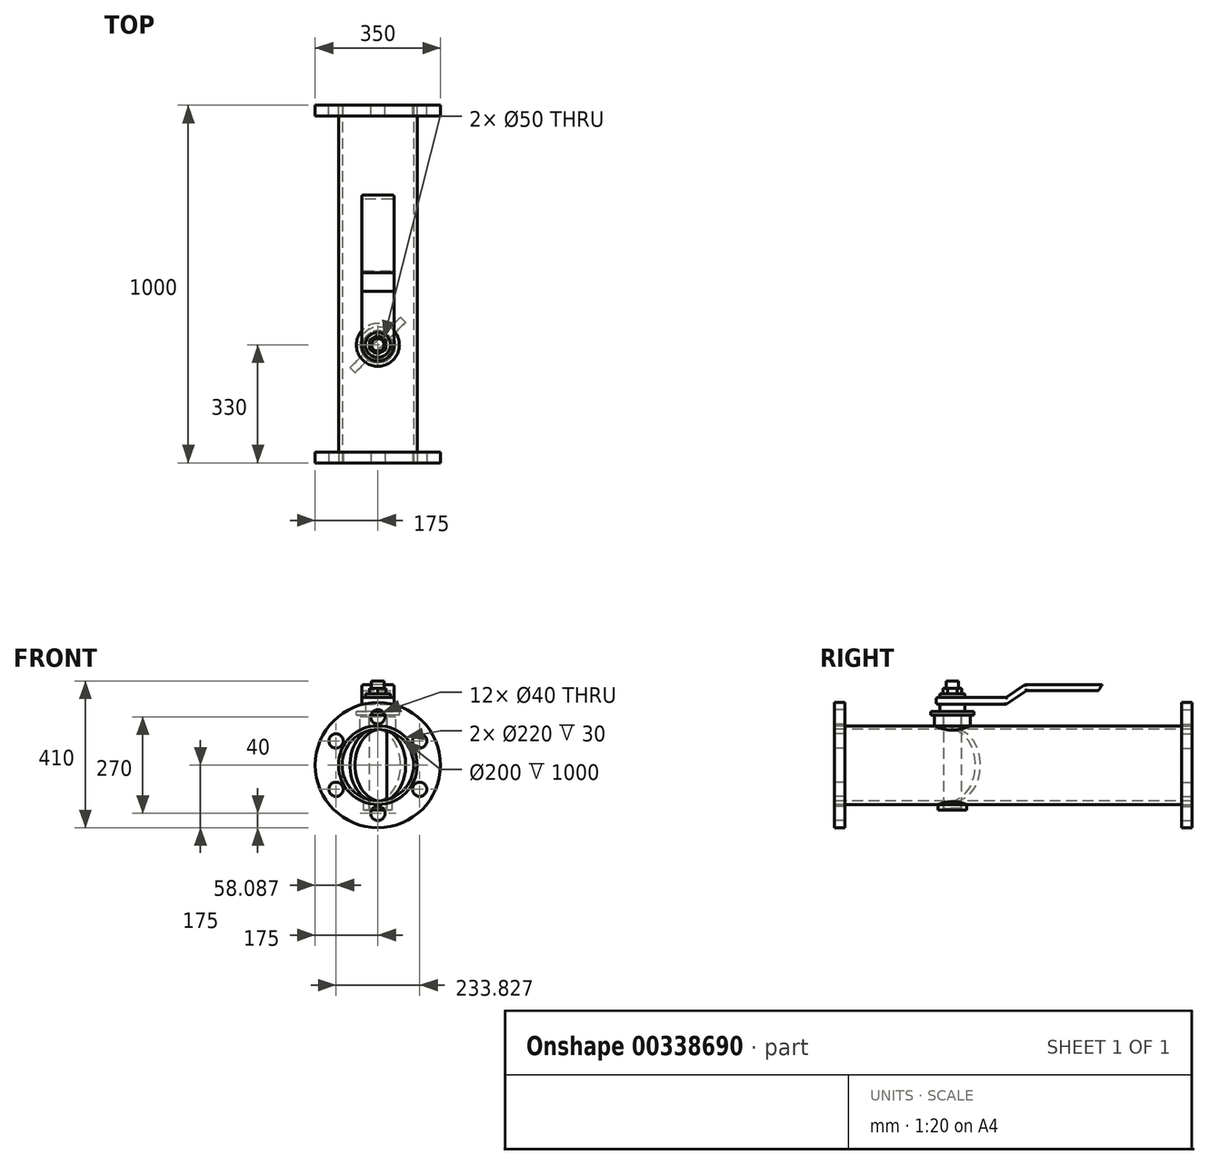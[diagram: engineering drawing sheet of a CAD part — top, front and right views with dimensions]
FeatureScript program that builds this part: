
annotation { "Feature Type Name" : "Feature", "Feature Type Description" : "" }
export const myFeature = defineFeature(function(context is Context, id is Id, definition is map)
    precondition{}
    {
        {
            var Q0;
            Q0=qCreatedBy(makeId("Front.planeOp"),FACE);
            var sketch = newSketch(context, id + "F0", { "sketchPlane" : qUnion([Q0])});
            skCircle(sketch, "E0", {"center": v(0, 0) * mm, "radius": 110 * mm});
            skSolve(sketch);
        }
        {
            var Q0;
            Q0=makeQuery(id+"F0.imprint","IMPRINT",FACE,{"disambiguationData":[TD([[makeQuery(id+"F0.imprint","IMPRINT",EDGE,{"derivedFrom":sQuery(id+"F0.wireOp",EDGE,"E0")}),1.0]])]});
            extrude(context, id + "F1", {"entities" : qUnion([Q0]), "oppositeDirection" : true, "depth" : 1000 * mm});
        }
        {
            var Q0;
            Q0=makeQuery(id+"F1.opExtrude","CAP_FACE",FACE,{"disambiguationData":[OSD([sQuery(id+"F0.wireOp",EDGE,"E0")])],"isStart":true});
            var sketch = newSketch(context, id + "F2", { "sketchPlane" : qUnion([Q0])});
            skCircle(sketch, "E1", {"center": v(0, 0) * mm, "radius": 175 * mm});
            skSolve(sketch);
        }
        {
            var Q0;
            Q0=makeQuery(id+"F2.imprint","IMPRINT",FACE,{"disambiguationData":[TD([[makeQuery(id+"F2.imprint","IMPRINT",EDGE,{"derivedFrom":sQuery(id+"F2.wireOp",EDGE,"E1")}),1.0]])]});
            extrude(context, id + "F3", {"entities" : qUnion([Q0]), "oppositeDirection" : true, "depth" : 30 * mm});
        }
        {
            var Q0;
            Q0=makeQuery(id+"F1.opExtrude","CAP_FACE",FACE,{"disambiguationData":[OSD([sQuery(id+"F0.wireOp",EDGE,"E0")])],"isStart":false});
            var sketch = newSketch(context, id + "F4", { "sketchPlane" : qUnion([Q0])});
            skCircle(sketch, "E2", {"center": v(0, 0) * mm, "radius": 175 * mm});
            skSolve(sketch);
        }
        {
            var Q0;
            Q0=makeQuery(id+"F4.imprint","IMPRINT",FACE,{"disambiguationData":[TD([[makeQuery(id+"F4.imprint","IMPRINT",EDGE,{"derivedFrom":sQuery(id+"F4.wireOp",EDGE,"E2")}),1.0]])]});
            extrude(context, id + "F5", {"entities" : qUnion([Q0]), "oppositeDirection" : true, "depth" : 30 * mm});
        }
        {
            var Q0;
            Q0=makeQuery(id+"F3.opExtrude","CAP_FACE",FACE,{"disambiguationData":[OSD([sQuery(id+"F0.wireOp",EDGE,"E0"),sQuery(id+"F2.wireOp",EDGE,"E1")])],"isStart":true});
            var sketch = newSketch(context, id + "F6", { "sketchPlane" : qUnion([Q0])});
            skCircle(sketch, "E3", {"center": v(0, 0) * mm, "radius": 100 * mm});
            skSolve(sketch);
        }
        {
            var Q0;
            Q0=makeQuery(id+"F6.imprint","IMPRINT",FACE,{"disambiguationData":[TD([[makeQuery(id+"F6.imprint","IMPRINT",EDGE,{"derivedFrom":sQuery(id+"F6.wireOp",EDGE,"E3")}),1.0]])]});
            extrude(context, id + "F7", {"entities" : qUnion([Q0]), "operationType" : NewBodyOperationType.REMOVE, "endBound" : BoundingType.THROUGH_ALL, "oppositeDirection" : true, "depth" : 25 * mm});
        }
        {
            var Q0;
            Q0=makeQuery(id+"F2.imprint","IMPRINT",FACE,{"disambiguationData":[TD([[makeQuery(id+"F2.imprint","IMPRINT",EDGE,{"derivedFrom":sQuery(id+"F2.wireOp",EDGE,"E1")}),1.0]])]});
            var sketch = newSketch(context, id + "F8", { "sketchPlane" : qUnion([Q0])});
            skCircle(sketch, "E4", {"center": v(0, 135) * mm, "radius": 20 * mm});
            skCircle(sketch, "E5.1.0", {"center": v(-116.91, 67.5) * mm, "radius": 20 * mm});
            skCircle(sketch, "E5.2.0", {"center": v(-116.91, -67.5) * mm, "radius": 20 * mm});
            skCircle(sketch, "E5.3.0", {"center": v(0, -135) * mm, "radius": 20 * mm});
            skCircle(sketch, "E5.4.0", {"center": v(116.91, -67.5) * mm, "radius": 20 * mm});
            skCircle(sketch, "E5.5.0", {"center": v(116.91, 67.5) * mm, "radius": 20 * mm});
            skPoint(sketch, "E5.center", {"position": v(0, 0) * mm});
            skSolve(sketch);
        }
        {
            var Q0;
            Q0 = qSketchRegion(id + "F8", true);
            var Q1;
            Q1=makeQuery(id+"F3.opExtrude","CAP_FACE",FACE,{"disambiguationData":[OSD([sQuery(id+"F0.wireOp",EDGE,"E0"),sQuery(id+"F2.wireOp",EDGE,"E1")])],"isStart":false});
            extrude(context, id + "F9", {"entities" : qUnion([Q0]), "operationType" : NewBodyOperationType.REMOVE, "endBound" : BoundingType.UP_TO_SURFACE, "oppositeDirection" : true, "endBoundEntityFace" : qUnion([Q1]), "depth" : 25 * mm});
        }
        {
            var Q0;
            Q0=makeQuery(id+"F4.imprint","IMPRINT",FACE,{"disambiguationData":[TD([[makeQuery(id+"F4.imprint","IMPRINT",EDGE,{"derivedFrom":sQuery(id+"F4.wireOp",EDGE,"E2")}),1.0]])]});
            var sketch = newSketch(context, id + "F10", { "sketchPlane" : qUnion([Q0])});
            skCircle(sketch, "E6", {"center": v(0, 135) * mm, "radius": 20 * mm});
            skCircle(sketch, "E7.1.0", {"center": v(-116.91, 67.5) * mm, "radius": 20 * mm});
            skCircle(sketch, "E7.2.0", {"center": v(-116.91, -67.5) * mm, "radius": 20 * mm});
            skCircle(sketch, "E7.3.0", {"center": v(0, -135) * mm, "radius": 20 * mm});
            skCircle(sketch, "E7.4.0", {"center": v(116.91, -67.5) * mm, "radius": 20 * mm});
            skCircle(sketch, "E7.5.0", {"center": v(116.91, 67.5) * mm, "radius": 20 * mm});
            skPoint(sketch, "E7.center", {"position": v(0, 0) * mm});
            skSolve(sketch);
        }
        {
            var Q0;
            Q0 = qSketchRegion(id + "F10", true);
            var Q1;
            Q1=makeQuery(id+"F5.opExtrude","CAP_FACE",FACE,{"disambiguationData":[OSD([sQuery(id+"F0.wireOp",EDGE,"E0"),sQuery(id+"F4.wireOp",EDGE,"E2")])],"isStart":false});
            extrude(context, id + "F11", {"entities" : qUnion([Q0]), "operationType" : NewBodyOperationType.REMOVE, "endBound" : BoundingType.UP_TO_SURFACE, "oppositeDirection" : true, "endBoundEntityFace" : qUnion([Q1]), "depth" : 25 * mm});
        }
        {
            var Q0;
            Q0=qCreatedBy(makeId("Front.planeOp"),FACE);
            cPlane(context, id + "F12", {"entities" : qUnion([Q0]), "cplaneType" : CPlaneType.OFFSET, "offset" : 330 * mm, "oppositeDirection" : true, "width" : 150 * mm, "height" : 150 * mm});
        }
        {
            var Q0;
            Q0=qCreatedBy(id+"F12.planeOp",FACE);
            var sketch = newSketch(context, id + "F13", { "sketchPlane" : qUnion([Q0])});
            skCircle(sketch, "E8", {"center": v(0, 0) * mm, "radius": 100 * mm});
            skSolve(sketch);
        }
        {
            var Q0;
            Q0 = qSketchRegion(id + "F13", true);
            extrude(context, id + "F14", {"entities" : qUnion([Q0]), "depth" : 10 * mm, "hasSecondDirection" : true, "secondDirectionOppositeDirection" : true, "secondDirectionDepth" : 10 * mm});
        }
        {
            var Q0;
            Q0=qCreatedBy(makeId("Top.planeOp"),FACE);
            var sketch = newSketch(context, id + "F15", { "sketchPlane" : qUnion([Q0])});
            skCircle(sketch, "E9", {"center": v(0, 330) * mm, "radius": 25 * mm});
            skSolve(sketch);
        }
        {
            var Q0;
            Q0 = qSketchRegion(id + "F15", true);
            extrude(context, id + "F16", {"entities" : qUnion([Q0]), "depth" : 150 * mm, "hasSecondDirection" : true, "secondDirectionOppositeDirection" : true, "secondDirectionDepth" : 120 * mm});
        }
        {
            var Q0;
            Q0=makeQuery(id+"F16.opExtrude","CAP_FACE",FACE,{"disambiguationData":[OSD([sQuery(id+"F15.wireOp",EDGE,"E9")])],"isStart":true});
            var sketch = newSketch(context, id + "F17", { "sketchPlane" : qUnion([Q0])});
            skCircle(sketch, "E10", {"center": v(0, -330) * mm, "radius": 40 * mm});
            skSolve(sketch);
        }
        {
            var Q0;
            Q0=makeQuery(id+"F17.imprint","IMPRINT",FACE,{"disambiguationData":[TD([[makeQuery(id+"F17.imprint","IMPRINT",EDGE,{"derivedFrom":sQuery(id+"F17.wireOp",EDGE,"E10")}),1.0]])]});
            var Q1;
            Q1=makeQuery(id+"F1.opExtrude","SWEPT_FACE",FACE,{"disambiguationData":[OSD([sQuery(id+"F0.wireOp",EDGE,"E0")])]});
            extrude(context, id + "F18", {"entities" : qUnion([Q0]), "depth" : 5 * mm, "hasSecondDirection" : true, "secondDirectionBound" : SecondDirectionBoundingType.UP_TO_SURFACE, "secondDirectionOppositeDirection" : true, "secondDirectionBoundEntityFace" : qUnion([Q1]), "secondDirectionDepth" : 25 * mm});
        }
        {
            var Q0;
            Q0=makeQuery(id+"F16.opExtrude","CAP_FACE",FACE,{"disambiguationData":[OSD([sQuery(id+"F15.wireOp",EDGE,"E9")])],"isStart":false});
            var sketch = newSketch(context, id + "F19", { "sketchPlane" : qUnion([Q0])});
            skCircle(sketch, "E11", {"center": v(0, 330) * mm, "radius": 60 * mm});
            skSolve(sketch);
        }
        {
            var Q0;
            Q0=makeQuery(id+"F19.imprint","IMPRINT",FACE,{"disambiguationData":[TD([[makeQuery(id+"F19.imprint","IMPRINT",EDGE,{"derivedFrom":sQuery(id+"F19.wireOp",EDGE,"E11")}),1.0]])]});
            extrude(context, id + "F20", {"entities" : qUnion([Q0]), "operationType" : NewBodyOperationType.ADD, "oppositeDirection" : true, "depth" : 10 * mm});
        }
        {
            var Q0;
            Q0=makeQuery(id+"F20.opExtrude","CAP_FACE",FACE,{"disambiguationData":[OSD([sQuery(id+"F15.wireOp",EDGE,"E9"),sQuery(id+"F19.wireOp",EDGE,"E11")])],"isStart":false});
            var sketch = newSketch(context, id + "F21", { "sketchPlane" : qUnion([Q0])});
            skCircle(sketch, "E12", {"center": v(0, -330) * mm, "radius": 50 * mm});
            skSolve(sketch);
        }
        {
            var Q0;
            Q0=makeQuery(id+"F21.imprint","IMPRINT",FACE,{"disambiguationData":[TD([[makeQuery(id+"F21.imprint","IMPRINT",EDGE,{"derivedFrom":sQuery(id+"F21.wireOp",EDGE,"E12")}),1.0]])]});
            var Q1;
            Q1=makeQuery(id+"F1.opExtrude","SWEPT_FACE",FACE,{"disambiguationData":[OSD([sQuery(id+"F0.wireOp",EDGE,"E0")])]});
            extrude(context, id + "F22", {"entities" : qUnion([Q0]), "endBound" : BoundingType.UP_TO_SURFACE, "endBoundEntityFace" : qUnion([Q1]), "depth" : 25 * mm});
        }
        {
            var Q0;
            {var subQ0=sQuery(id+"F15.wireOp",EDGE,"E9");Q0=makeQuery(id+"F20.boolean.opBoolean","MERGE",FACE,{"derivedFrom":[makeQuery(id+"F16.opExtrude","CAP_FACE",FACE,{"disambiguationData":[OSD([subQ0])],"isStart":false}),makeQuery(id+"F20.opExtrude","CAP_FACE",FACE,{"disambiguationData":[OSD([subQ0,sQuery(id+"F19.wireOp",EDGE,"E11")])],"isStart":true})]});}
            var sketch = newSketch(context, id + "F23", { "sketchPlane" : qUnion([Q0])});
            skCircle(sketch, "E13", {"center": v(0, 330) * mm, "radius": 35 * mm});
            skSolve(sketch);
        }
        {
            var Q0;
            Q0=makeQuery(id+"F23.imprint","IMPRINT",FACE,{"disambiguationData":[TD([[makeQuery(id+"F23.imprint","IMPRINT",EDGE,{"derivedFrom":sQuery(id+"F23.wireOp",EDGE,"E13")}),1.0]])]});
            extrude(context, id + "F24", {"entities" : qUnion([Q0]), "operationType" : NewBodyOperationType.ADD, "depth" : 50 * mm});
        }
        {
            var Q0;
            Q0=makeQuery(id+"F24.opExtrude","CAP_FACE",FACE,{"disambiguationData":[OSD([sQuery(id+"F23.wireOp",EDGE,"E13")])],"isStart":false});
            var sketch = newSketch(context, id + "F25", { "sketchPlane" : qUnion([Q0])});
            skCircle(sketch, "E14", {"center": v(0, 330) * mm, "radius": 17.5 * mm});
            skSolve(sketch);
        }
        {
            var Q0;
            Q0=makeQuery(id+"F25.imprint","IMPRINT",FACE,{"disambiguationData":[TD([[makeQuery(id+"F25.imprint","IMPRINT",EDGE,{"derivedFrom":sQuery(id+"F25.wireOp",EDGE,"E14")}),1.0]])]});
            extrude(context, id + "F26", {"entities" : qUnion([Q0]), "operationType" : NewBodyOperationType.ADD, "depth" : 35 * mm});
        }
        {
            var Q0;
            Q0=makeQuery(id+"F24.opExtrude","CAP_FACE",FACE,{"disambiguationData":[OSD([sQuery(id+"F23.wireOp",EDGE,"E13")])],"isStart":false});
            var sketch = newSketch(context, id + "F27", { "sketchPlane" : qUnion([Q0])});
            skCircle(sketch, "E15.cCircle", {"center": v(0, 330) * mm, "radius": 22.6 * mm, "construction": true});
            skLineSegment(sketch, "E15.0", {"start": v(-22.6, 316.96) * mm, "end": v(-22.6, 343.04) * mm});
            skLineSegment(sketch, "E15.1", {"start": v(-22.6, 343.04) * mm, "end": v(0, 356.09) * mm});
            skLineSegment(sketch, "E15.2", {"start": v(0, 356.09) * mm, "end": v(22.6, 343.04) * mm});
            skLineSegment(sketch, "E15.3", {"start": v(22.6, 343.04) * mm, "end": v(22.6, 316.96) * mm});
            skLineSegment(sketch, "E15.4", {"start": v(22.6, 316.96) * mm, "end": v(0, 303.91) * mm});
            skLineSegment(sketch, "E15.5", {"start": v(0, 303.91) * mm, "end": v(-22.6, 316.96) * mm});
            skPoint(sketch, "E15.0.midPoint", {"position": v(-22.6, 330) * mm});
            skSolve(sketch);
        }
        {
            var Q0;
            Q0=makeQuery(id+"F27.imprint","IMPRINT",FACE,{"disambiguationData":[TD([[makeQuery(id+"F27.imprint","IMPRINT",EDGE,{"derivedFrom":sQuery(id+"F27.wireOp",EDGE,"E15.0")}),-1.0]])]});
            extrude(context, id + "F28", {"entities" : qUnion([Q0]), "operationType" : NewBodyOperationType.ADD, "depth" : 15 * mm});
        }
        {
            var Q0;
            {var subQ0=sQuery(id+"F15.wireOp",EDGE,"E9");Q0=makeQuery(id+"F20.boolean.opBoolean","MERGE",FACE,{"derivedFrom":[makeQuery(id+"F16.opExtrude","CAP_FACE",FACE,{"disambiguationData":[OSD([subQ0])],"isStart":false}),makeQuery(id+"F20.opExtrude","CAP_FACE",FACE,{"disambiguationData":[OSD([subQ0,sQuery(id+"F19.wireOp",EDGE,"E11")])],"isStart":true})]});}
            cPlane(context, id + "F29", {"entities" : qUnion([Q0]), "cplaneType" : CPlaneType.OFFSET, "offset" : 20 * mm, "width" : 150 * mm, "height" : 150 * mm});
        }
        {
            var Q0;
            Q0=qCreatedBy(id+"F29.planeOp",FACE);
            var sketch = newSketch(context, id + "F30", { "sketchPlane" : qUnion([Q0])});
            skArc(sketch, "E16", {"start": v(-45, 330) * mm, "mid": v(0, 285) * mm, "end": v(45, 330) * mm});
            skLineSegment(sketch, "E17", {"start": v(45, 330) * mm, "end": v(45, 480) * mm});
            skLineSegment(sketch, "E18", {"start": v(45, 480) * mm, "end": v(-45, 480) * mm});
            skLineSegment(sketch, "E19", {"start": v(-45, 480) * mm, "end": v(-45, 330) * mm});
            skSolve(sketch);
        }
        {
            var Q0;
            Q0=makeQuery(id+"F30.imprint","IMPRINT",FACE,{"disambiguationData":[TD([[makeQuery(id+"F30.imprint","IMPRINT",EDGE,{"derivedFrom":sQuery(id+"F30.wireOp",EDGE,"E16")}),1.0]])]});
            extrude(context, id + "F31", {"entities" : qUnion([Q0]), "operationType" : NewBodyOperationType.ADD, "depth" : 20 * mm});
        }
        {
            var Q0;
            Q0=makeQuery(id+"F31.opExtrude","SWEPT_FACE",FACE,{"disambiguationData":[OSD([sQuery(id+"F30.wireOp",EDGE,"E17")])]});
            var sketch = newSketch(context, id + "F32", { "sketchPlane" : qUnion([Q0])});
            skLineSegment(sketch, "E20", {"start": v(480, 190) * mm, "end": v(532.26, 224.92) * mm});
            skLineSegment(sketch, "E21", {"start": v(532.26, 224.92) * mm, "end": v(748.87, 224.92) * mm});
            skSolve(sketch);
        }
        {
            var Q0;
            Q0=makeQuery(id+"F31.opExtrude","SWEPT_FACE",FACE,{"disambiguationData":[OSD([sQuery(id+"F30.wireOp",EDGE,"E18")])]});
            var Q1;
            Q1=sQuery(id+"F32.wireOp",EDGE,"E20");
            var Q2;
            Q2=sQuery(id+"F32.wireOp",EDGE,"E21");
            sweep(context, id + "F33", {"operationType" : NewBodyOperationType.ADD, "profiles" : qUnion([Q0]), "path" : qUnion([Q1, Q2])});
        }
        {
            var Q0;
            {var subQ0=sQuery(id+"F32.wireOp",EDGE,"E21");var subQ1=sQuery(id+"F30.wireOp",EDGE,"E18");var subQ2=sQuery(id+"F30.wireOp",EDGE,"E17");Q0=makeQuery(id+"F33.opSweep","SWEPT_EDGE",EDGE,{"disambiguationData":[OSD([subQ2,subQ1,subQ0]),TDD([makeQuery(id+"F31.opExtrude","CAP_VERTEX",VERTEX,{"disambiguationData":[OSD([subQ2,subQ1])],"isStart":false}),subQ0])]});}
            var Q1;
            {var subQ0=sQuery(id+"F32.wireOp",EDGE,"E20");var subQ1=sQuery(id+"F30.wireOp",EDGE,"E18");var subQ2=sQuery(id+"F30.wireOp",EDGE,"E17");Q1=makeQuery(id+"F33.opSweep","SWEPT_EDGE",EDGE,{"disambiguationData":[OSD([subQ2,subQ1,subQ0]),TDD([makeQuery(id+"F31.opExtrude","CAP_VERTEX",VERTEX,{"disambiguationData":[OSD([subQ2,subQ1])],"isStart":false}),subQ0])]});}
            var Q2;
            Q2=makeQuery(id+"F31.opExtrude","CAP_EDGE",EDGE,{"disambiguationData":[OSD([sQuery(id+"F30.wireOp",EDGE,"E17")])],"isStart":false});
            var Q3;
            Q3=makeQuery(id+"F31.opExtrude","CAP_EDGE",EDGE,{"disambiguationData":[OSD([sQuery(id+"F30.wireOp",EDGE,"E17")])],"isStart":true});
            var Q4;
            {var subQ0=sQuery(id+"F32.wireOp",EDGE,"E20");var subQ1=sQuery(id+"F30.wireOp",EDGE,"E18");var subQ2=sQuery(id+"F30.wireOp",EDGE,"E17");Q4=makeQuery(id+"F33.opSweep","SWEPT_EDGE",EDGE,{"disambiguationData":[OSD([subQ2,subQ1,subQ0]),TDD([makeQuery(id+"F31.opExtrude","CAP_VERTEX",VERTEX,{"disambiguationData":[OSD([subQ2,subQ1])],"isStart":true}),subQ0])]});}
            var Q5;
            {var subQ0=sQuery(id+"F32.wireOp",EDGE,"E21");var subQ1=sQuery(id+"F30.wireOp",EDGE,"E18");var subQ2=sQuery(id+"F30.wireOp",EDGE,"E17");Q5=makeQuery(id+"F33.opSweep","SWEPT_EDGE",EDGE,{"disambiguationData":[OSD([subQ2,subQ1,subQ0]),TDD([makeQuery(id+"F31.opExtrude","CAP_VERTEX",VERTEX,{"disambiguationData":[OSD([subQ2,subQ1])],"isStart":true}),subQ0])]});}
            var Q6;
            {var subQ0=sQuery(id+"F32.wireOp",EDGE,"E20");var subQ1=sQuery(id+"F30.wireOp",EDGE,"E19");var subQ2=sQuery(id+"F30.wireOp",EDGE,"E18");Q6=makeQuery(id+"F33.opSweep","SWEPT_EDGE",EDGE,{"disambiguationData":[OSD([subQ2,subQ1,subQ0]),TDD([makeQuery(id+"F31.opExtrude","CAP_VERTEX",VERTEX,{"disambiguationData":[OSD([subQ2,subQ1])],"isStart":false}),subQ0])]});}
            var Q7;
            {var subQ0=sQuery(id+"F32.wireOp",EDGE,"E21");var subQ1=sQuery(id+"F30.wireOp",EDGE,"E19");var subQ2=sQuery(id+"F30.wireOp",EDGE,"E18");Q7=makeQuery(id+"F33.opSweep","SWEPT_EDGE",EDGE,{"disambiguationData":[OSD([subQ2,subQ1,subQ0]),TDD([makeQuery(id+"F31.opExtrude","CAP_VERTEX",VERTEX,{"disambiguationData":[OSD([subQ2,subQ1])],"isStart":false}),subQ0])]});}
            var Q8;
            {var subQ0=sQuery(id+"F32.wireOp",EDGE,"E20");var subQ1=sQuery(id+"F30.wireOp",EDGE,"E19");var subQ2=sQuery(id+"F30.wireOp",EDGE,"E18");Q8=makeQuery(id+"F33.opSweep","SWEPT_EDGE",EDGE,{"disambiguationData":[OSD([subQ2,subQ1,subQ0]),TDD([makeQuery(id+"F31.opExtrude","CAP_VERTEX",VERTEX,{"disambiguationData":[OSD([subQ2,subQ1])],"isStart":true}),subQ0])]});}
            var Q9;
            {var subQ0=sQuery(id+"F32.wireOp",EDGE,"E21");var subQ1=sQuery(id+"F30.wireOp",EDGE,"E19");var subQ2=sQuery(id+"F30.wireOp",EDGE,"E18");Q9=makeQuery(id+"F33.opSweep","SWEPT_EDGE",EDGE,{"disambiguationData":[OSD([subQ2,subQ1,subQ0]),TDD([makeQuery(id+"F31.opExtrude","CAP_VERTEX",VERTEX,{"disambiguationData":[OSD([subQ2,subQ1])],"isStart":true}),subQ0])]});}
            fillet(context, id + "F34", {"entities" : qUnion([Q0, Q1, Q2, Q3, Q4, Q5, Q6, Q7, Q8, Q9]), "radius" : 5 * mm, "tangentPropagation" : true, "allowEdgeOverflow" : false});
        }
        {
            var Q0;
            Q0=qCreatedBy(makeId("Right.planeOp"),FACE);
            var sketch = newSketch(context, id + "F35", { "sketchPlane" : qUnion([Q0])});
            skLineSegment(sketch, "E22.0", {"start": v(312.5, 235) * mm, "end": v(347.5, 235) * mm, "construction": true});
            skPoint(sketch, "E23", {"position": v(330, 235) * mm});
            skLineSegment(sketch, "E24", {"start": v(330, 235) * mm, "end": v(330, -145.43) * mm, "construction": true});
            skSolve(sketch);
        }
        {
            var Q0;
            Q0=makeQuery(id+"F14.opExtrude","SWEPT_BODY",BODY,{"disambiguationData":[OSD([sQuery(id+"F13.wireOp",EDGE,"E8")])]});
            var Q1;
            Q1=sQuery(id+"F35.wireOp",EDGE,"E24");
            transform(context, id + "F36", {"entities" : qUnion([Q0]), "transformType" : TransformType.ROTATION, "transformAxis" : qUnion([Q1]), "angle" : 45 * degree, "oppositeDirection" : true, "makeCopy" : false});
        }
    });
